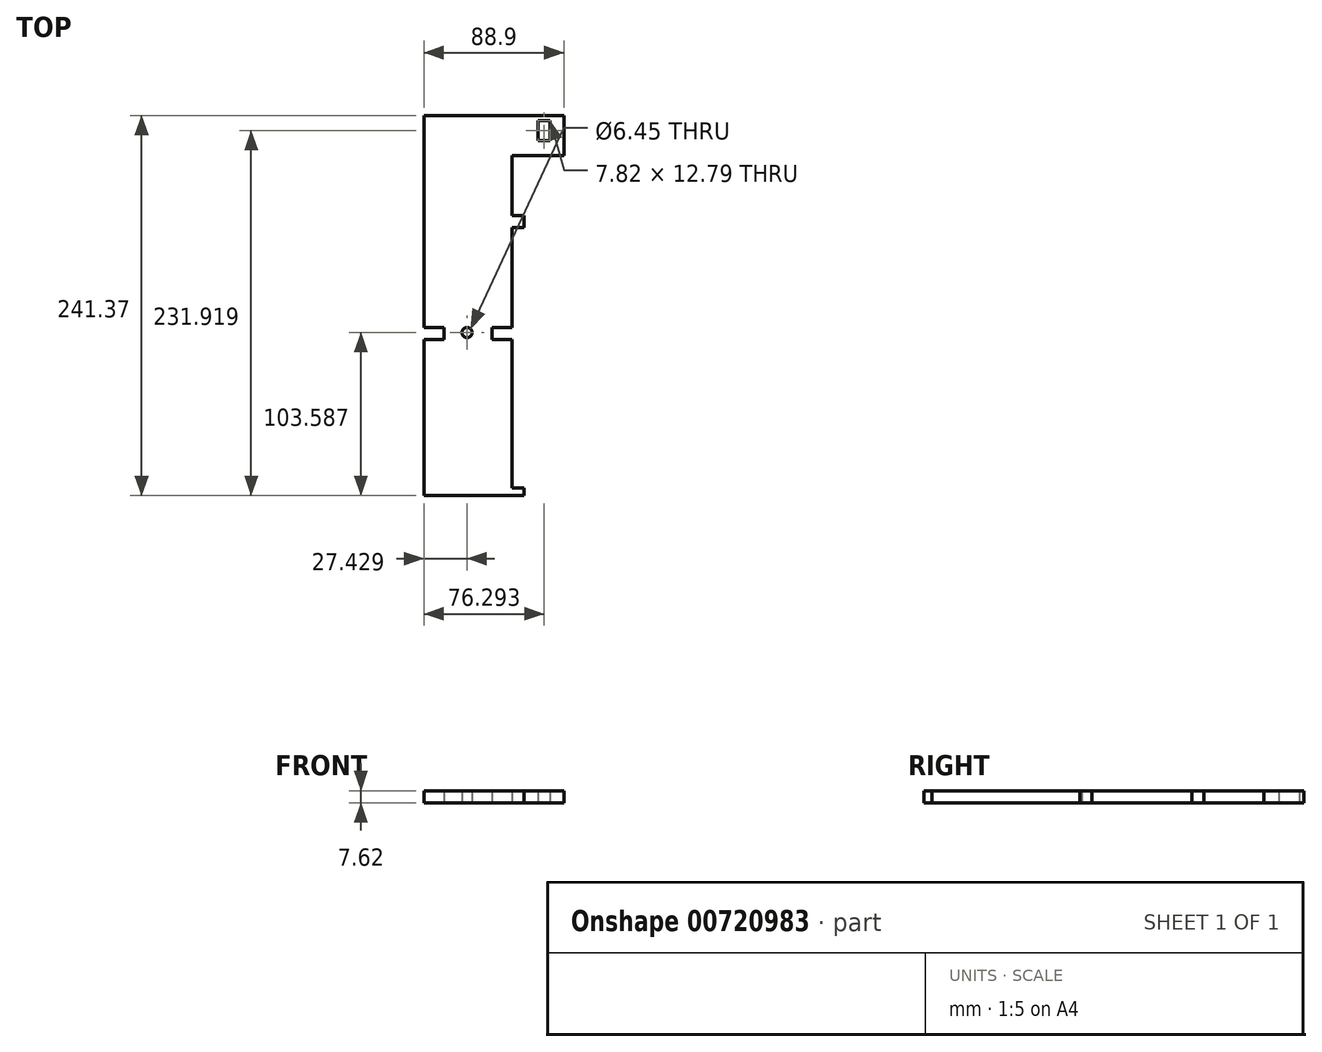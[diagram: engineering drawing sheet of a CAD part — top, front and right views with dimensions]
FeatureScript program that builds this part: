
annotation { "Feature Type Name" : "Feature", "Feature Type Description" : "" }
export const myFeature = defineFeature(function(context is Context, id is Id, definition is map)
    precondition{}
    {
        {
            var Q0;
            Q0=qCreatedBy(makeId("Top.planeOp"),FACE);
            var sketch = newSketch(context, id + "F0", { "sketchPlane" : qUnion([Q0])});
            skLineSegment(sketch, "E0", {"start": v(-50.22, 163.74) * mm, "end": v(38.68, 163.74) * mm});
            skLineSegment(sketch, "E1", {"start": v(38.68, 163.74) * mm, "end": v(38.68, 138.34) * mm});
            skLineSegment(sketch, "E2", {"start": v(38.68, 138.34) * mm, "end": v(5.66, 138.34) * mm});
            skLineSegment(sketch, "E3", {"start": v(5.66, 138.34) * mm, "end": v(5.66, 100.24) * mm});
            skLineSegment(sketch, "E4", {"start": v(5.66, 100.24) * mm, "end": v(13.28, 100.24) * mm});
            skLineSegment(sketch, "E5", {"start": v(13.28, 100.24) * mm, "end": v(13.28, 92.62) * mm});
            skLineSegment(sketch, "E6", {"start": v(13.28, 92.62) * mm, "end": v(5.66, 92.62) * mm});
            skLineSegment(sketch, "E7", {"start": v(5.66, 92.62) * mm, "end": v(5.66, 29.12) * mm});
            skLineSegment(sketch, "E8", {"start": v(5.66, 29.12) * mm, "end": v(-7.04, 29.12) * mm});
            skLineSegment(sketch, "E9", {"start": v(-7.04, 29.12) * mm, "end": v(-7.04, 21.5) * mm});
            skLineSegment(sketch, "E10", {"start": v(-7.04, 21.5) * mm, "end": v(5.66, 21.5) * mm});
            skLineSegment(sketch, "E11", {"start": v(5.66, 21.5) * mm, "end": v(5.66, -62.32) * mm});
            skLineSegment(sketch, "E12", {"start": v(5.66, -62.32) * mm, "end": v(5.66, -72.67) * mm});
            skLineSegment(sketch, "E13", {"start": v(5.66, -72.67) * mm, "end": v(13.28, -72.67) * mm});
            skLineSegment(sketch, "E14", {"start": v(13.28, -72.67) * mm, "end": v(13.28, -77.63) * mm});
            skLineSegment(sketch, "E15", {"start": v(13.28, -77.63) * mm, "end": v(-50.22, -77.63) * mm});
            skLineSegment(sketch, "E16", {"start": v(-50.22, -77.63) * mm, "end": v(-50.22, 21.5) * mm});
            skLineSegment(sketch, "E17", {"start": v(-50.22, 21.5) * mm, "end": v(-37.52, 21.5) * mm});
            skLineSegment(sketch, "E18", {"start": v(-37.52, 21.5) * mm, "end": v(-37.52, 29.12) * mm});
            skLineSegment(sketch, "E19", {"start": v(-37.52, 29.12) * mm, "end": v(-50.22, 29.12) * mm});
            skLineSegment(sketch, "E20", {"start": v(-50.22, 29.12) * mm, "end": v(-50.22, 163.74) * mm});
            skCircle(sketch, "E21", {"center": v(-22.8, 25.96) * mm, "radius": 3.22 * mm});
            skLineSegment(sketch, "E22", {"start": v(22.16, 160.68) * mm, "end": v(22.16, 147.9) * mm});
            skLineSegment(sketch, "E23", {"start": v(22.16, 147.9) * mm, "end": v(29.99, 147.9) * mm});
            skLineSegment(sketch, "E24", {"start": v(29.99, 147.9) * mm, "end": v(29.99, 160.68) * mm});
            skLineSegment(sketch, "E25", {"start": v(29.99, 160.68) * mm, "end": v(22.16, 160.68) * mm});
            skSolve(sketch);
        }
        {
            var Q0;
            Q0 = qSketchRegion(id + "F0", true);
            extrude(context, id + "F1", {"entities" : qUnion([Q0]), "depth" : 7.62 * mm, "offsetDistance" : 25.4 * mm});
        }
    });
